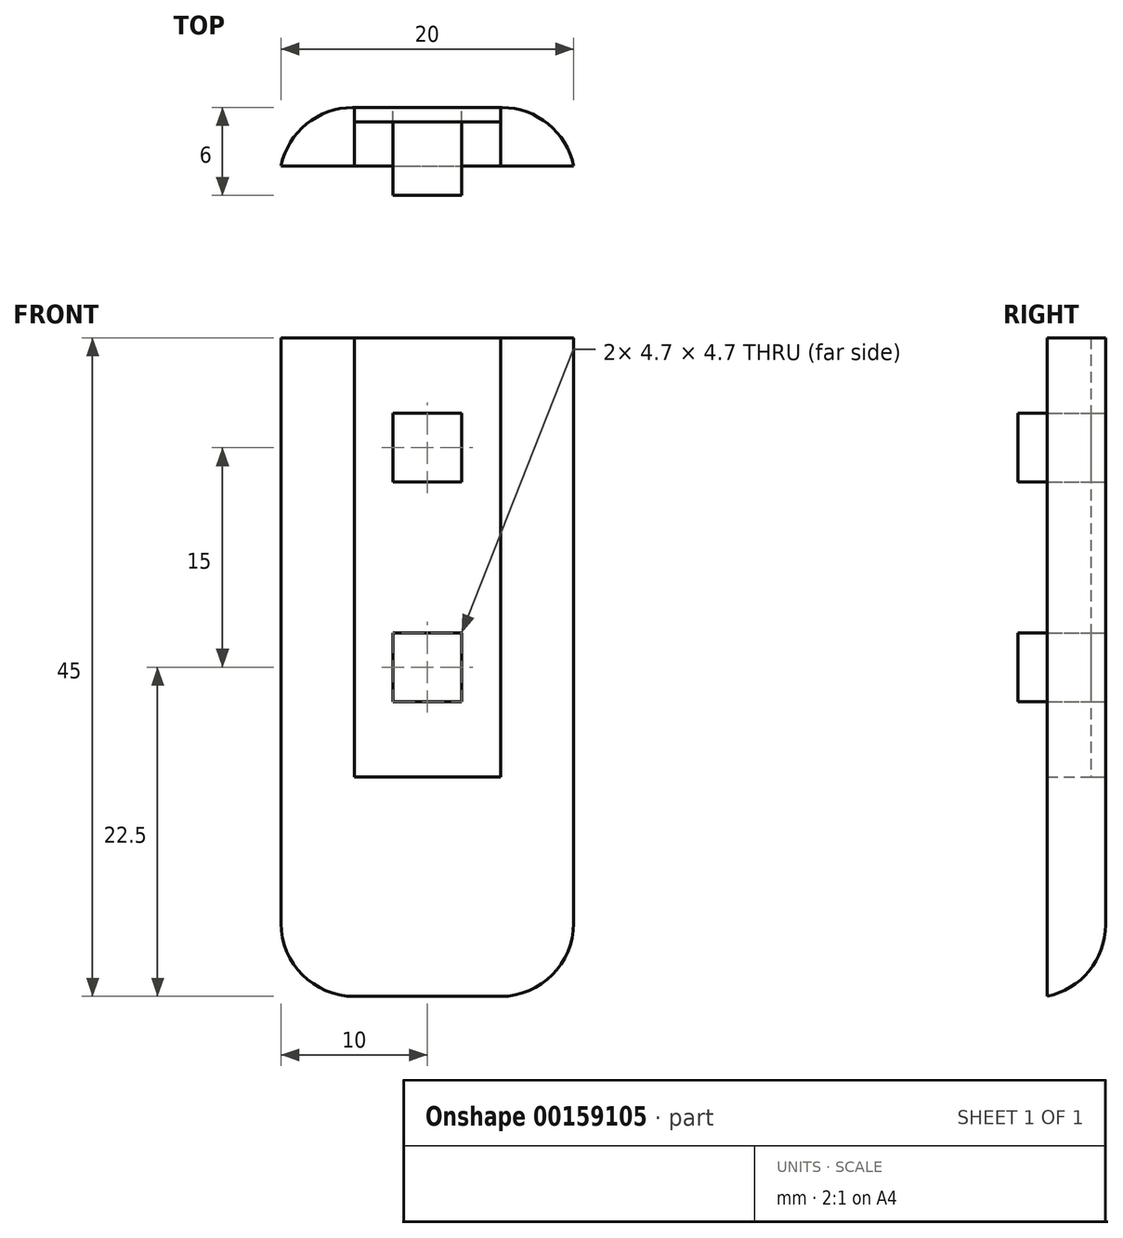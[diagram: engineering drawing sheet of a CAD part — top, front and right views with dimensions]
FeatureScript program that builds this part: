
annotation { "Feature Type Name" : "Feature", "Feature Type Description" : "" }
export const myFeature = defineFeature(function(context is Context, id is Id, definition is map)
    precondition{}
    {
        {
            var Q0;
            Q0=qCreatedBy(makeId("Front.planeOp"),FACE);
            var sketch = newSketch(context, id + "F0", { "sketchPlane" : qUnion([Q0])});
            skLineSegment(sketch, "E0.bottom", {"start": v(-5, -22.5) * mm, "end": v(5, -22.5) * mm});
            skLineSegment(sketch, "E0.top", {"start": v(-10, 22.5) * mm, "end": v(10, 22.5) * mm});
            skLineSegment(sketch, "E0.left", {"start": v(-10, -17.5) * mm, "end": v(-10, 22.5) * mm});
            skLineSegment(sketch, "E0.right", {"start": v(10, -17.5) * mm, "end": v(10, 22.5) * mm});
            skPoint(sketch, "E0.middle", {"position": v(0, 0) * mm});
            skPoint(sketch, "E1.visualSharp", {"position": v(-10, -22.5) * mm});
            skArc(sketch, "E1.filletArc", {"start": v(-10, -17.5) * mm, "mid": v(-8.54, -21.04) * mm, "end": v(-5, -22.5) * mm});
            skPoint(sketch, "E2.visualSharp", {"position": v(10, -22.5) * mm});
            skArc(sketch, "E2.filletArc", {"start": v(5, -22.5) * mm, "mid": v(8.54, -21.04) * mm, "end": v(10, -17.5) * mm});
            skPoint(sketch, "E3.middle", {"position": v(0, 15) * mm});
            skPoint(sketch, "E3.top.start.orphan", {"position": v(-2.5, 12.5) * mm});
            skPoint(sketch, "E3.right.end.orphan", {"position": v(2.35, 12.65) * mm});
            skPoint(sketch, "E3.bottom.end.orphan", {"position": v(2.5, 17.5) * mm});
            skPoint(sketch, "E3.bottom.start.orphan", {"position": v(-2.35, 17.35) * mm});
            skLineSegment(sketch, "E4.bottom", {"start": v(-2.35, 17.35) * mm, "end": v(2.35, 17.35) * mm});
            skLineSegment(sketch, "E4.top", {"start": v(-2.35, 12.65) * mm, "end": v(2.35, 12.65) * mm});
            skLineSegment(sketch, "E4.left", {"start": v(-2.35, 17.35) * mm, "end": v(-2.35, 12.65) * mm});
            skLineSegment(sketch, "E4.right", {"start": v(2.35, 17.35) * mm, "end": v(2.35, 12.65) * mm});
            skPoint(sketch, "E5.left.end.orphan", {"position": v(-2.35, -2.35) * mm});
            skPoint(sketch, "E5.left.start.orphan", {"position": v(-2.35, 28.19) * mm});
            skPoint(sketch, "E5.right.end.orphan", {"position": v(2.35, -28.19) * mm});
            skPoint(sketch, "E5.right.start.orphan", {"position": v(2.35, 2.35) * mm});
            skLineSegment(sketch, "E6.bottom", {"start": v(2.35, 2.35) * mm, "end": v(-2.35, 2.35) * mm});
            skLineSegment(sketch, "E6.top", {"start": v(2.35, -2.35) * mm, "end": v(-2.35, -2.35) * mm});
            skLineSegment(sketch, "E6.left", {"start": v(2.35, 2.35) * mm, "end": v(2.35, -2.35) * mm});
            skLineSegment(sketch, "E6.right", {"start": v(-2.35, 2.35) * mm, "end": v(-2.35, -2.35) * mm});
            skLineSegment(sketch, "E7", {"start": v(0, 22.5) * mm, "end": v(0, 0) * mm, "construction": true});
            skLineSegment(sketch, "E8.bottom", {"start": v(-5, 22.5) * mm, "end": v(5, 22.5) * mm});
            skLineSegment(sketch, "E8.top", {"start": v(-5, -7.5) * mm, "end": v(5, -7.5) * mm});
            skLineSegment(sketch, "E8.left", {"start": v(-5, 22.5) * mm, "end": v(-5, -7.5) * mm});
            skLineSegment(sketch, "E8.right", {"start": v(5, 22.5) * mm, "end": v(5, -7.5) * mm});
            skSolve(sketch);
        }
        {
            var Q0;
            Q0=makeQuery(id+"F0.imprint","IMPRINT",FACE,{"disambiguationData":[TD([[makeQuery(id+"F0.imprint","IMPRINT",EDGE,{"derivedFrom":sQuery(id+"F0.wireOp",EDGE,"E0.bottom")}),1.0]])]});
            extrude(context, id + "F1", {"entities" : qUnion([Q0]), "depth" : 4 * mm});
        }
        {
            var Q0;
            Q0=makeQuery(id+"F1.opExtrude","CAP_EDGE",EDGE,{"disambiguationData":[OSD([sQuery(id+"F0.wireOp",EDGE,"E0.right")])],"isStart":true});
            fillet(context, id + "F2", {"entities" : qUnion([Q0]), "radius" : 5 * mm, "tangentPropagation" : true, "allowEdgeOverflow" : false});
        }
        {
            var Q0;
            Q0=makeQuery(id+"F0.imprint","IMPRINT",FACE,{"disambiguationData":[TD([[makeQuery(id+"F0.imprint","IMPRINT",EDGE,{"derivedFrom":sQuery(id+"F0.wireOp",EDGE,"E6.bottom")}),1.0]])]});
            var Q1;
            Q1=makeQuery(id+"F0.imprint","IMPRINT",FACE,{"disambiguationData":[TD([[makeQuery(id+"F0.imprint","IMPRINT",EDGE,{"derivedFrom":sQuery(id+"F0.wireOp",EDGE,"E4.bottom")}),-1.0]])]});
            extrude(context, id + "F3", {"entities" : qUnion([Q0, Q1]), "operationType" : NewBodyOperationType.ADD, "depth" : 6 * mm});
        }
        {
            var Q0;
            Q0=makeQuery(id+"F0.imprint","IMPRINT",FACE,{"disambiguationData":[TD([[makeQuery(id+"F0.imprint","IMPRINT",EDGE,{"derivedFrom":sQuery(id+"F0.wireOp",EDGE,"E4.bottom")}),1.0]])]});
            extrude(context, id + "F4", {"entities" : qUnion([Q0]), "depth" : 1 * mm});
        }
    });
